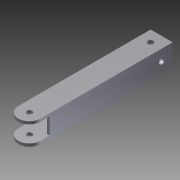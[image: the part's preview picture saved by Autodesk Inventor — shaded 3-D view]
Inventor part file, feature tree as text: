
AUTODESK INVENTOR PART (.ipt)
format: ipt  version: 2012 (Build 160160000, 160)  size: 117,760 bytes
history: native  units: in
note: dims shown in document units (in); Inventor stores cm internally (conversion verified against a paired STEP export)
features: extrude x3, sketch x3
ambient origin geometry x8: Origin, YZ Plane, XZ Plane, XY Plane, X Axis, Y Axis, Z Axis, Center Point
bodies: Solid1 (feature_tree)
feature tree (6):
  extrude  "Extrusion1"  Depth=0.125in
  extrude  "Extrusion2"  Depth=0.125in
  extrude  "Extrusion3"  Depth=1.0in
  sketch  "Sketch1"  dims[d0=0.125in d1=0.125in]
  sketch  "Sketch2"  dims[d2=0.125in d3=0.125in]
  sketch  "Sketch3"  dims[d4=1.0in d5=1.0in d6=6.5in d7=0.0in d8=0.25in d9=6.5in d10=0.0in d11=0.75in d12=0.25in d13=0.5in d14=0.5in d15=6.5in d16=0.0in d17=0.5in d18=0.25in]
